# Revit family: UL924 Flush Mount Emergency Load Control Relay
name_source: partatom
category: Communication Devices
revit_build: Autodesk Revit 2014 (Build: 20130308_1515(x64)
units: mm (PartAtom-declared; Revit-internal decimal feet)

## types (1)
- UL924 Flush Mount Emergency Load Control Relay
    Application = •Outdoor Lighting
•Parking Lot
•Parking Garage
•Commerical
•Education
•Healthcare
•Hospitality
•Manufacturing
•Retail
•Warehouse
    Assembly Code = D5090
    Default Elevation = 48 "
    Description = Hubbell Control Solutions flush mount 20 amp emergency load control relay is specifically designed for applications that require the control of emergency light fixtures along with the general lighting in a space. This type of emergency lighting is often referred to as “always on”. The UL924EPC1-UNV connects to the line side of the control device to sense the presence of “normal” power. It also connects to the load side of the control device to provide an ON/OFF signal for control of the emergency lights along with the general lighting. When normal power is lost, control is suspended and the normally closed relay provides emergency power to the emergency fixtures
    Features = •20 Amp, normally closed relay
•120 or 277 volt operation
•UL924 Listed
•LED power indicators
•Integral test button
•No minimum load requirement
•UL94-V5A rated plastic
•Five-year warranty
    Gray = Paint - Hubbell - Gray Smooth
    Green = Paint - Hubbell - Green Textured
    Height = 4.5 "
    Manufacturer = Hubbell Control Solutions
    Model = UL924EPC1-UNV
    Product Documentation Link = https://hubbellcdn.com
    Product Page URL = https://www.hubbell.com
    Red = Paint - Hubbell - Red
    Type Comments = UL924 Flush Mount Relay
    URL = https://www.hubbell.com
    Warranty = 5-Years Warranty
    Width = 2.75 "

## geometry (parser evidence)
native form markers: Sweep x1
no freeform markers — native parametric forms only
